# Revit family: PRD_AR_TltRllHldrs_RODANToiletRollHolder_RODX672,674B
name_source: partatom
category: Specialty Equipment
revit_build: Autodesk Revit 2018 (Build: 20190510_1515(x64)
units: mm (PartAtom-declared; Revit-internal decimal feet)

## family parameters
Cut with Voids When Loaded = No
Host = Face
OmniClass Number = 23.40.20.21.21
OmniClass Title = Toilet Paper Dispensers
Part Type = Normal
Room Calculation Point = No
Round Connector Dimension = Use Diameter
Shared = No

## types (2) — shared parameters
AssetType = Fixed
Category = Pr_40_20_76_88, Toilet roll holders
Color = Stainless steel
Default Elevation = 700 mm  [stored 2.29659 ft]
DurationUnit = year
Finish = Satin finished
FinishAndColour = Stainless steel, satin finished
Form = Wall mounting
IfcExportAs = IfcFurnitureType
IfcExportType = NOTDEFINED
IntegralAccessories = incl. stainless steel screws and dowels
MainColor = Stainless steel
Manufacturer = KWC Group AG
ManufacturerName = KWC Group AG
ManufacturerURL = www.kwc.com
Material = Stainless steel
MaterialCode = Stainless steel 1.4301
Materials = Stainless steel
NBSDescription = Toilet roll holders
NBSReference = 45-35-72/368
ProductInformation = https://pim.kwc.com
RollHolderMaterial = PRD_AR_StainlessSteel_SatinFinished
Style = Toilet roll holder
ToiletRollMaterial = PRD_AR_ToiletRoll
URL = www.kwc.com
Uniclass2015Code = Pr_40_20_76_88
Uniclass2015Title = Toilet roll holders
Uniclass2015Version = Products v1.10
Version = 1
WarrantyDurationUnit = year

## per-type parameters (varying)
| type | BIMObjectName | Description | Features | FillingQuantity | GrossWeight | MaximumWidthOfConsumable | ModelNumber | Name | NetWeight | NominalDepth | NominalHeight | NominalWidth | Size |
| RODX672 | PRD_AR_ToiletRollHolders_RODAN_ToiletRollHolder_RODX672 | Double toilet roll holder with spindle system for wall mounting, stainless steel, surface satin finished, material thickness 0.8 mm, folded front cover, cylinder lock with KWC standard key, for 2 rolls with max. ⌀120 mm, second roll will be released after consumption of first roll, with spindles, reserve roll not visible, incl. stainless steel screws and dowels. | stainless steel, 0.80 mm, satin finished, wall mounting, 144x301x138 mm (WxHxD) | 2 Rolls | 2.42 kg | 115 mm  [stored 0.377297 ft] | 2000090072 | RODAN Double toilet roll holder RODX672 | 2.15 kg | 138 mm  [stored 0.452756 ft] | 301 mm  [stored 0.987533 ft] | 144 mm  [stored 0.472441 ft] | 144x301x138 mm |
| RODX674B | PRD_AR_ToiletRollHolders_RODAN_DoubleToiletRollHolder_RODX674B | Toilet roll holder for 4 rolls for wall mounting, stainless steel, surface satin finished, material thickness 0.8 mm, with spindle system, cylinder lock with KWC standard key, incl. stainless steel screws and dowels. | stainless steel, 0.80 mm, satin finished, wall mounting, 145x610x144 mm (WxHxD) | 4 Rolls | 5.62 kg | 110 mm  [stored 0.360892 ft] | 2030002104 | RODAN Double toilet roll holder RODX674B | 4.98 kg | 144 mm  [stored 0.472441 ft] | 610 mm  [stored 2.00131 ft] | 145 mm  [stored 0.475722 ft] | 144x610x145 mm |

note: column(s) folded — value = type name in every type: Model, ModelReference, Type

note: [stored X ft] marks values corroborated as IEEE doubles in the binary element streams (Revit-internal decimal feet)

## geometry (parser evidence)
native form markers: Sweep x8
no freeform markers — native parametric forms only
